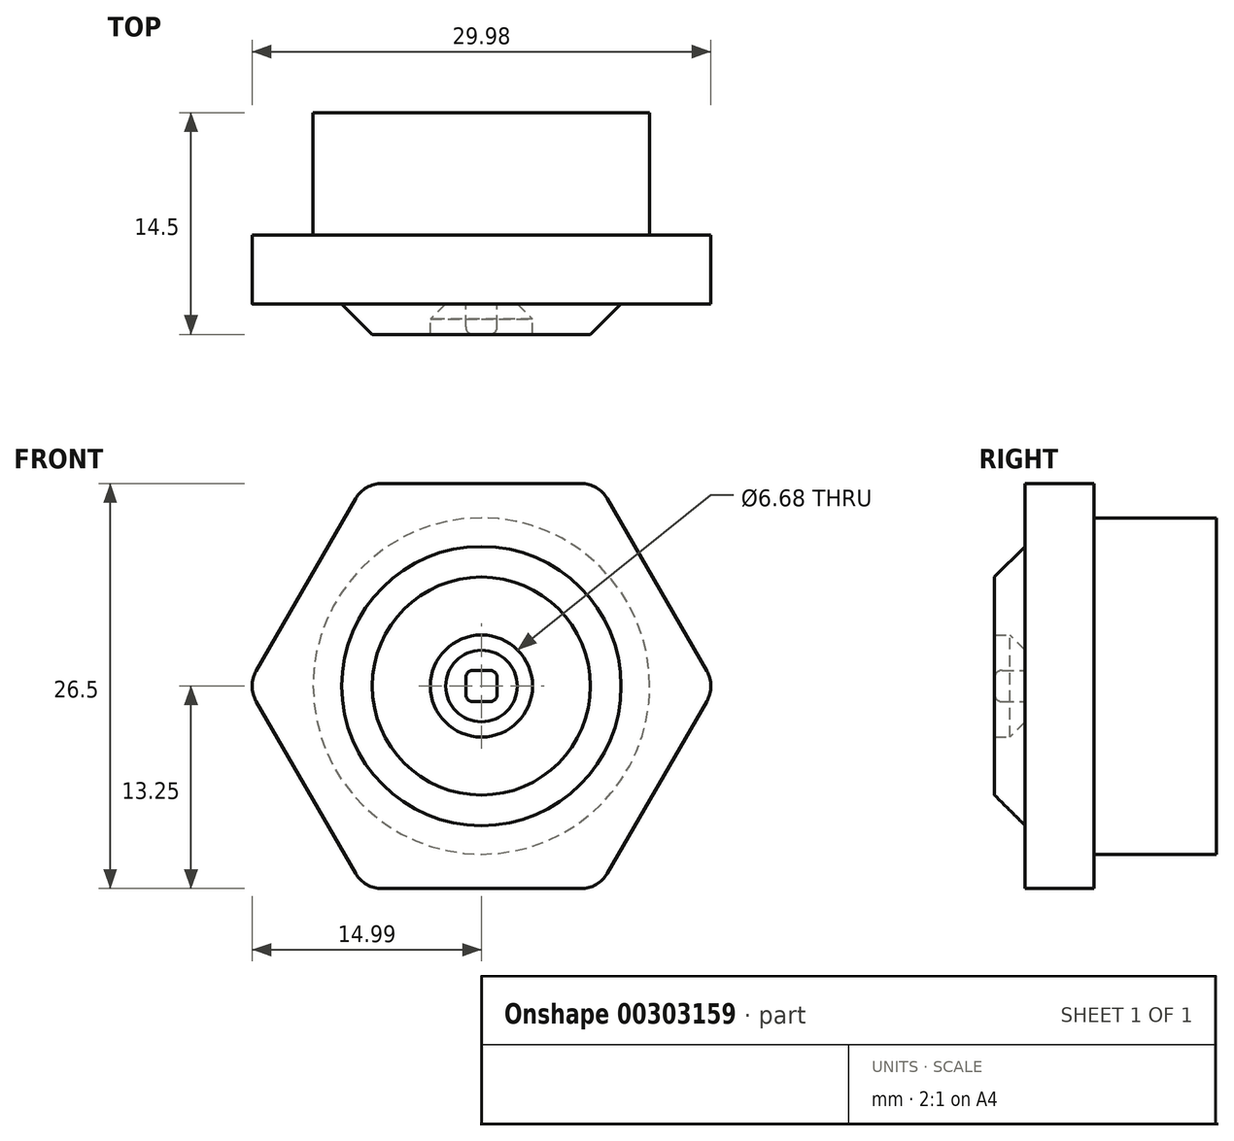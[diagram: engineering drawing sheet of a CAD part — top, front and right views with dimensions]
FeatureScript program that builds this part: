
annotation { "Feature Type Name" : "Feature", "Feature Type Description" : "" }
export const myFeature = defineFeature(function(context is Context, id is Id, definition is map)
    precondition{}
    {
        {
            var Q0;
            Q0=qCreatedBy(makeId("Front.planeOp"),FACE);
            var sketch = newSketch(context, id + "F0", { "sketchPlane" : qUnion([Q0])});
            skCircle(sketch, "E0", {"center": v(0, 0) * mm, "radius": 11 * mm});
            skSolve(sketch);
        }
        {
            var Q0;
            Q0 = qSketchRegion(id + "F0", true);
            extrude(context, id + "F1", {"entities" : qUnion([Q0]), "depth" : 8 * mm});
        }
        {
            var Q0;
            Q0=makeQuery(id+"F1.opExtrude","CAP_FACE",FACE,{"disambiguationData":[OSD([sQuery(id+"F0.wireOp",EDGE,"E0")])],"isStart":false});
            var sketch = newSketch(context, id + "F2", { "sketchPlane" : qUnion([Q0])});
            skCircle(sketch, "E1.cCircle", {"center": v(0, 0) * mm, "radius": 13.25 * mm, "construction": true});
            skLineSegment(sketch, "E1.0", {"start": v(-6.5, 13.25) * mm, "end": v(6.5, 13.25) * mm});
            skLineSegment(sketch, "E1.1", {"start": v(8.23, 12.25) * mm, "end": v(14.72, 1) * mm});
            skLineSegment(sketch, "E1.2", {"start": v(14.72, -1) * mm, "end": v(8.23, -12.25) * mm});
            skLineSegment(sketch, "E1.3", {"start": v(6.5, -13.25) * mm, "end": v(-6.5, -13.25) * mm});
            skLineSegment(sketch, "E1.4", {"start": v(-8.23, -12.25) * mm, "end": v(-14.72, -1) * mm});
            skLineSegment(sketch, "E1.5", {"start": v(-14.72, 1) * mm, "end": v(-8.23, 12.25) * mm});
            skPoint(sketch, "E1.0.midPoint", {"position": v(0, 13.25) * mm});
            skPoint(sketch, "E2.visualSharp", {"position": v(-7.65, 13.25) * mm});
            skArc(sketch, "E2.filletArc", {"start": v(-6.5, 13.25) * mm, "mid": v(-7.5, 12.98) * mm, "end": v(-8.23, 12.25) * mm});
            skPoint(sketch, "E3.visualSharp", {"position": v(7.65, 13.25) * mm});
            skArc(sketch, "E3.filletArc", {"start": v(8.23, 12.25) * mm, "mid": v(7.5, 12.98) * mm, "end": v(6.5, 13.25) * mm});
            skPoint(sketch, "E4.visualSharp", {"position": v(15.3, 0) * mm});
            skArc(sketch, "E4.filletArc", {"start": v(14.72, -1) * mm, "mid": v(15, 0) * mm, "end": v(14.72, 1) * mm});
            skPoint(sketch, "E5.visualSharp", {"position": v(7.65, -13.25) * mm});
            skArc(sketch, "E5.filletArc", {"start": v(6.5, -13.25) * mm, "mid": v(7.5, -12.98) * mm, "end": v(8.23, -12.25) * mm});
            skPoint(sketch, "E6.visualSharp", {"position": v(-7.65, -13.25) * mm});
            skArc(sketch, "E6.filletArc", {"start": v(-8.23, -12.25) * mm, "mid": v(-7.5, -12.98) * mm, "end": v(-6.5, -13.25) * mm});
            skPoint(sketch, "E7.visualSharp", {"position": v(-15.3, 0) * mm});
            skArc(sketch, "E7.filletArc", {"start": v(-14.72, 1) * mm, "mid": v(-15, 0) * mm, "end": v(-14.72, -1) * mm});
            skSolve(sketch);
        }
        {
            var Q0;
            Q0 = qSketchRegion(id + "F2", true);
            extrude(context, id + "F3", {"entities" : qUnion([Q0]), "operationType" : NewBodyOperationType.ADD, "depth" : 4.5 * mm});
        }
        {
            var Q0;
            Q0=makeQuery(id+"F3.opExtrude","CAP_FACE",FACE,{"disambiguationData":[OSD([sQuery(id+"F2.wireOp",EDGE,"E1.0"),sQuery(id+"F2.wireOp",EDGE,"E1.1"),sQuery(id+"F2.wireOp",EDGE,"E1.2"),sQuery(id+"F2.wireOp",EDGE,"E1.3"),sQuery(id+"F2.wireOp",EDGE,"E1.4"),sQuery(id+"F2.wireOp",EDGE,"E1.5")])],"isStart":false});
            var sketch = newSketch(context, id + "F4", { "sketchPlane" : qUnion([Q0])});
            skCircle(sketch, "E8", {"center": v(0, 0) * mm, "radius": 3.34 * mm});
            skCircle(sketch, "E9", {"center": v(0, 0) * mm, "radius": 12.13 * mm});
            skSolve(sketch);
        }
        {
            var Q0;
            Q0 = qSketchRegion(id + "F4", true);
            extrude(context, id + "F5", {"entities" : qUnion([Q0]), "operationType" : NewBodyOperationType.ADD, "depth" : 2 * mm});
        }
        {
            var Q0;
            Q0=makeQuery(id+"F5.opExtrude","CAP_EDGE",EDGE,{"disambiguationData":[OSD([sQuery(id+"F4.wireOp",EDGE,"E9")])],"isStart":false});
            chamfer(context, id + "F6", {"entities" : qUnion([Q0]), "width" : 5 * mm, "tangentPropagation" : true});
        }
        {
            var Q0;
            Q0=makeQuery(id+"F5.boolean.opBoolean","SPLIT",FACE,{"disambiguationData":[TD([makeQuery(id+"F5.opExtrude","SWEPT_FACE",FACE,{"disambiguationData":[OSD([sQuery(id+"F4.wireOp",EDGE,"E8")])]})])],"derivedFrom":makeQuery(id+"F3.opExtrude","CAP_FACE",FACE,{"disambiguationData":[OSD([sQuery(id+"F2.wireOp",EDGE,"E1.0"),sQuery(id+"F2.wireOp",EDGE,"E1.1"),sQuery(id+"F2.wireOp",EDGE,"E1.2"),sQuery(id+"F2.wireOp",EDGE,"E1.3"),sQuery(id+"F2.wireOp",EDGE,"E1.4"),sQuery(id+"F2.wireOp",EDGE,"E1.5")])],"isStart":false})});
            chamfer(context, id + "F7", {"entities" : qUnion([Q0]), "width" : 1 * mm, "tangentPropagation" : true});
        }
        {
            var Q0;
            Q0=makeQuery(id+"F5.boolean.opBoolean","SPLIT",FACE,{"disambiguationData":[TD([makeQuery(id+"F5.opExtrude","SWEPT_FACE",FACE,{"disambiguationData":[OSD([sQuery(id+"F4.wireOp",EDGE,"E8")])]})])],"derivedFrom":makeQuery(id+"F3.opExtrude","CAP_FACE",FACE,{"disambiguationData":[OSD([sQuery(id+"F2.wireOp",EDGE,"E1.0"),sQuery(id+"F2.wireOp",EDGE,"E1.1"),sQuery(id+"F2.wireOp",EDGE,"E1.2"),sQuery(id+"F2.wireOp",EDGE,"E1.3"),sQuery(id+"F2.wireOp",EDGE,"E1.4"),sQuery(id+"F2.wireOp",EDGE,"E1.5")])],"isStart":false})});
            var sketch = newSketch(context, id + "F8", { "sketchPlane" : qUnion([Q0])});
            skLineSegment(sketch, "E10.bottom", {"start": v(1.03, 1.03) * mm, "end": v(-1.03, 1.03) * mm});
            skLineSegment(sketch, "E10.top", {"start": v(1.03, -1.03) * mm, "end": v(-1.03, -1.03) * mm});
            skLineSegment(sketch, "E10.left", {"start": v(1.03, 1.03) * mm, "end": v(1.03, -1.03) * mm});
            skLineSegment(sketch, "E10.right", {"start": v(-1.03, 1.03) * mm, "end": v(-1.03, -1.03) * mm});
            skPoint(sketch, "E10.middle", {"position": v(0, 0) * mm});
            skSolve(sketch);
        }
        {
            var Q0;
            Q0 = qSketchRegion(id + "F8", true);
            extrude(context, id + "F9", {"entities" : qUnion([Q0]), "operationType" : NewBodyOperationType.ADD, "depth" : 2 * mm});
        }
        {
            var Q0;
            Q0=makeQuery(id+"F9.opExtrude","SWEPT_EDGE",EDGE,{"disambiguationData":[OSD([sQuery(id+"F8.wireOp",EDGE,"E10.top"),sQuery(id+"F8.wireOp",EDGE,"E10.left")])]});
            var Q1;
            Q1=makeQuery(id+"F9.opExtrude","SWEPT_EDGE",EDGE,{"disambiguationData":[OSD([sQuery(id+"F8.wireOp",EDGE,"E10.top"),sQuery(id+"F8.wireOp",EDGE,"E10.right")])]});
            var Q2;
            Q2=makeQuery(id+"F9.opExtrude","SWEPT_EDGE",EDGE,{"disambiguationData":[OSD([sQuery(id+"F8.wireOp",EDGE,"E10.bottom"),sQuery(id+"F8.wireOp",EDGE,"E10.right")])]});
            var Q3;
            Q3=makeQuery(id+"F9.opExtrude","SWEPT_EDGE",EDGE,{"disambiguationData":[OSD([sQuery(id+"F8.wireOp",EDGE,"E10.bottom"),sQuery(id+"F8.wireOp",EDGE,"E10.left")])]});
            var Q4;
            Q4=makeQuery(id+"F9.opExtrude","CAP_FACE",FACE,{"disambiguationData":[OSD([sQuery(id+"F8.wireOp",EDGE,"E10.bottom"),sQuery(id+"F8.wireOp",EDGE,"E10.top"),sQuery(id+"F8.wireOp",EDGE,"E10.left"),sQuery(id+"F8.wireOp",EDGE,"E10.right")])],"isStart":false});
            fillet(context, id + "F10", {"entities" : qUnion([Q0, Q1, Q2, Q3, Q4]), "radius" : 0.5 * mm, "tangentPropagation" : true, "allowEdgeOverflow" : false});
        }
    });
